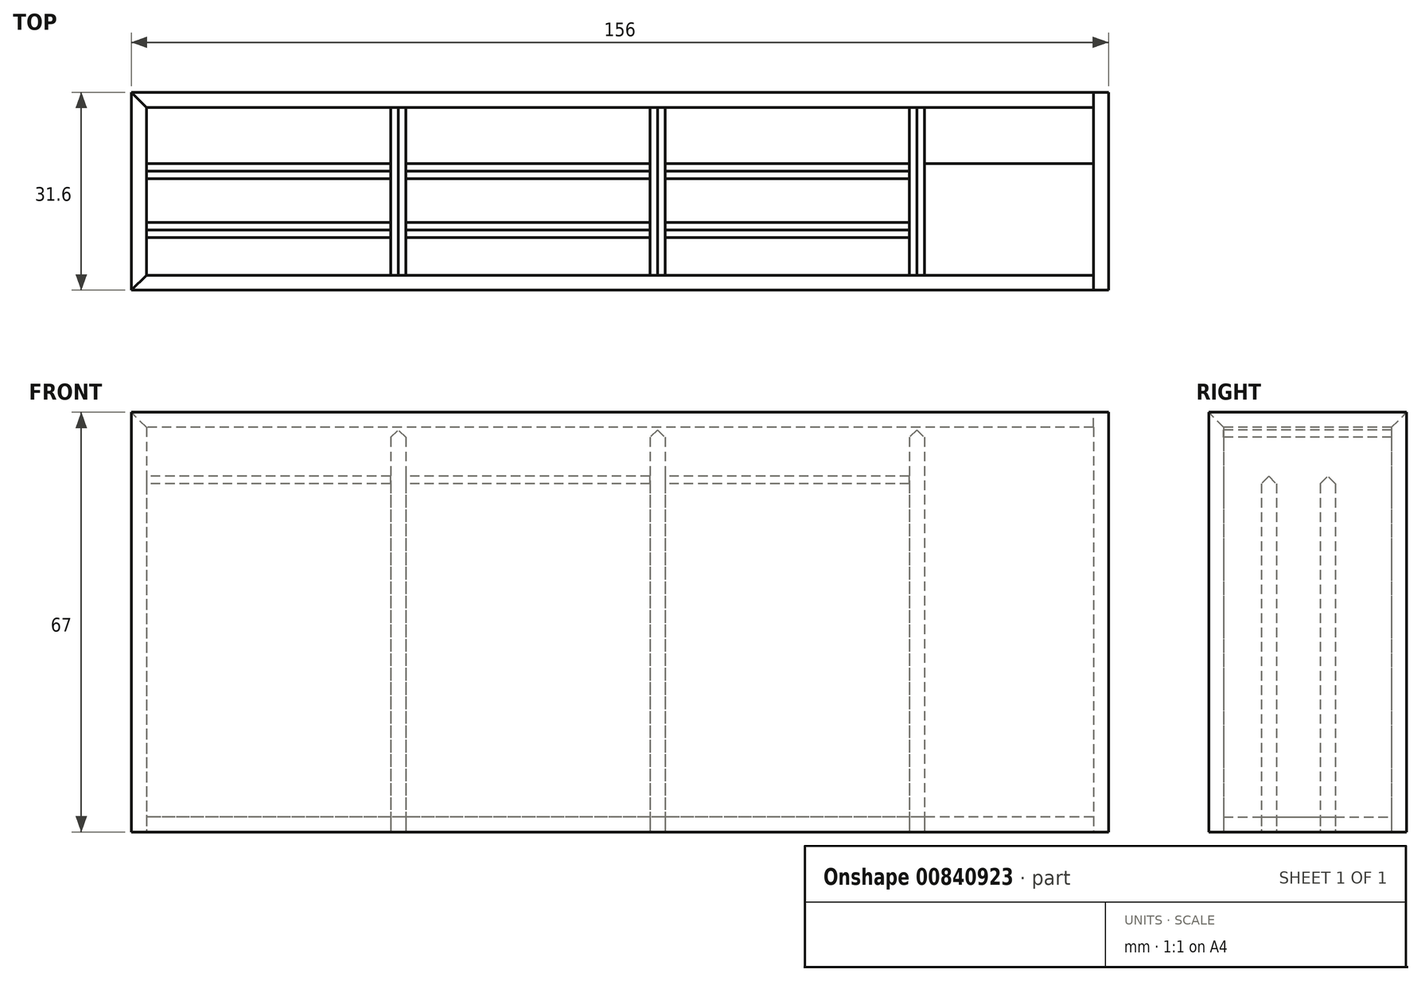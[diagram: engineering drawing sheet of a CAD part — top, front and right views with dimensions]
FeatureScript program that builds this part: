
annotation { "Feature Type Name" : "Feature", "Feature Type Description" : "" }
export const myFeature = defineFeature(function(context is Context, id is Id, definition is map)
    precondition{}
    {
        {
            var Q0;
            Q0=qCreatedBy(makeId("Top.planeOp"),FACE);
            var sketch = newSketch(context, id + "F0", { "sketchPlane" : qUnion([Q0])});
            skLineSegment(sketch, "E0.bottom", {"start": v(78, -15.8) * mm, "end": v(-78, -15.8) * mm});
            skLineSegment(sketch, "E0.top", {"start": v(78, 15.8) * mm, "end": v(-78, 15.8) * mm});
            skLineSegment(sketch, "E0.left", {"start": v(78, -15.8) * mm, "end": v(78, 15.8) * mm});
            skLineSegment(sketch, "E0.right", {"start": v(-78, -15.8) * mm, "end": v(-78, 15.8) * mm});
            skLineSegment(sketch, "E1.0", {"start": v(75.6, 13.4) * mm, "end": v(-75.6, 13.4) * mm});
            skLineSegment(sketch, "E1.1", {"start": v(75.6, -13.4) * mm, "end": v(75.6, 13.4) * mm});
            skLineSegment(sketch, "E1.2", {"start": v(75.6, -13.4) * mm, "end": v(-75.6, -13.4) * mm});
            skLineSegment(sketch, "E1.3", {"start": v(-75.6, -13.4) * mm, "end": v(-75.6, 13.4) * mm});
            skLineSegment(sketch, "E2.0", {"start": v(-36.6, -13.4) * mm, "end": v(-36.6, 13.4) * mm});
            skLineSegment(sketch, "E3.0", {"start": v(-34.2, -13.4) * mm, "end": v(-34.2, 13.4) * mm});
            skLineSegment(sketch, "E4.0", {"start": v(4.8, -13.4) * mm, "end": v(4.8, 13.4) * mm});
            skLineSegment(sketch, "E5.0", {"start": v(7.2, -13.4) * mm, "end": v(7.2, 13.4) * mm});
            skLineSegment(sketch, "E6.0", {"start": v(46.2, -13.4) * mm, "end": v(46.2, 13.4) * mm});
            skLineSegment(sketch, "E7.0", {"start": v(48.6, -13.4) * mm, "end": v(48.6, 13.4) * mm});
            skLineSegment(sketch, "E8", {"start": v(48.6, 13.4) * mm, "end": v(75.6, 13.4) * mm});
            skLineSegment(sketch, "E9.0", {"start": v(75.6, -7.4) * mm, "end": v(-75.6, -7.4) * mm});
            skLineSegment(sketch, "E10.0", {"start": v(75.6, -5) * mm, "end": v(-75.6, -5) * mm});
            skLineSegment(sketch, "E11.0", {"start": v(75.6, 2) * mm, "end": v(-75.6, 2) * mm});
            skLineSegment(sketch, "E12.0", {"start": v(75.6, 4.4) * mm, "end": v(-75.6, 4.4) * mm});
            skLineSegment(sketch, "E13", {"start": v(75.6, 13.4) * mm, "end": v(75.6, -13.4) * mm});
            skSolve(sketch);
        }
        {
            var Q0;
            Q0=makeQuery(id+"F0.imprint","IMPRINT",FACE,{"disambiguationData":[TD([[makeQuery(id+"F0.imprint","IMPRINT",EDGE,{"derivedFrom":sQuery(id+"F0.wireOp",EDGE,"E0.bottom")}),-1.0]])]});
            extrude(context, id + "F1", {"entities" : qUnion([Q0]), "depth" : 67 * mm, "offsetDistance" : 25 * mm});
        }
        {
            var Q0;
            {var subQ0=sQuery(id+"F0.wireOp",EDGE,"E6.0");var subQ1=sQuery(id+"F0.wireOp",EDGE,"E1.2");var subQ2=makeQuery(id+"F0.imprint","INTERSECT",VERTEX,{"derivedFrom":[subQ1,subQ0]});Q0=makeQuery(id+"F0.imprint","IMPRINT",FACE,{"disambiguationData":[TD([[makeQuery(id+"F0.imprint","IMPRINT",EDGE,{"disambiguationData":[TD([[subQ2,1.0]])],"derivedFrom":subQ1}),-1.0]])]});}
            var Q1;
            {var subQ0=sQuery(id+"F0.wireOp",EDGE,"E9.0");var subQ1=sQuery(id+"F0.wireOp",EDGE,"E6.0");var subQ2=makeQuery(id+"F0.imprint","INTERSECT",VERTEX,{"derivedFrom":[subQ1,subQ0]});Q1=makeQuery(id+"F0.imprint","IMPRINT",FACE,{"disambiguationData":[TD([[makeQuery(id+"F0.imprint","IMPRINT",EDGE,{"disambiguationData":[TD([[subQ2,-1.0]])],"derivedFrom":subQ1}),-1.0]])]});}
            var Q2;
            {var subQ0=sQuery(id+"F0.wireOp",EDGE,"E10.0");var subQ1=sQuery(id+"F0.wireOp",EDGE,"E6.0");var subQ2=makeQuery(id+"F0.imprint","INTERSECT",VERTEX,{"derivedFrom":[subQ1,subQ0]});Q2=makeQuery(id+"F0.imprint","IMPRINT",FACE,{"disambiguationData":[TD([[makeQuery(id+"F0.imprint","IMPRINT",EDGE,{"disambiguationData":[TD([[subQ2,-1.0]])],"derivedFrom":subQ1}),-1.0]])]});}
            var Q3;
            {var subQ0=sQuery(id+"F0.wireOp",EDGE,"E11.0");var subQ1=sQuery(id+"F0.wireOp",EDGE,"E6.0");var subQ2=makeQuery(id+"F0.imprint","INTERSECT",VERTEX,{"derivedFrom":[subQ1,subQ0]});Q3=makeQuery(id+"F0.imprint","IMPRINT",FACE,{"disambiguationData":[TD([[makeQuery(id+"F0.imprint","IMPRINT",EDGE,{"disambiguationData":[TD([[subQ2,-1.0]])],"derivedFrom":subQ1}),-1.0]])]});}
            var Q4;
            {var subQ1=sQuery(id+"F0.wireOp",EDGE,"E1.0");var subQ3=sQuery(id+"F0.wireOp",EDGE,"E6.0");var subQ4=makeQuery(id+"F0.imprint","INTERSECT",VERTEX,{"derivedFrom":[subQ1,subQ3]});Q4=makeQuery(id+"F0.imprint","IMPRINT",FACE,{"disambiguationData":[TD([[makeQuery(id+"F0.imprint","IMPRINT",EDGE,{"disambiguationData":[TD([[subQ4,1.0]])],"derivedFrom":subQ3}),-1.0]])]});}
            var Q5;
            {var subQ0=sQuery(id+"F0.wireOp",EDGE,"E4.0");var subQ1=sQuery(id+"F0.wireOp",EDGE,"E1.0");var subQ2=makeQuery(id+"F0.imprint","INTERSECT",VERTEX,{"derivedFrom":[subQ1,subQ0]});Q5=makeQuery(id+"F0.imprint","IMPRINT",FACE,{"disambiguationData":[TD([[makeQuery(id+"F0.imprint","IMPRINT",EDGE,{"disambiguationData":[TD([[subQ2,1.0]])],"derivedFrom":subQ1}),1.0]])]});}
            var Q6;
            {var subQ0=sQuery(id+"F0.wireOp",EDGE,"E11.0");var subQ1=sQuery(id+"F0.wireOp",EDGE,"E4.0");var subQ2=makeQuery(id+"F0.imprint","INTERSECT",VERTEX,{"derivedFrom":[subQ1,subQ0]});Q6=makeQuery(id+"F0.imprint","IMPRINT",FACE,{"disambiguationData":[TD([[makeQuery(id+"F0.imprint","IMPRINT",EDGE,{"disambiguationData":[TD([[subQ2,-1.0]])],"derivedFrom":subQ1}),-1.0]])]});}
            var Q7;
            {var subQ0=sQuery(id+"F0.wireOp",EDGE,"E10.0");var subQ1=sQuery(id+"F0.wireOp",EDGE,"E4.0");var subQ2=makeQuery(id+"F0.imprint","INTERSECT",VERTEX,{"derivedFrom":[subQ1,subQ0]});Q7=makeQuery(id+"F0.imprint","IMPRINT",FACE,{"disambiguationData":[TD([[makeQuery(id+"F0.imprint","IMPRINT",EDGE,{"disambiguationData":[TD([[subQ2,-1.0]])],"derivedFrom":subQ1}),-1.0]])]});}
            var Q8;
            {var subQ0=sQuery(id+"F0.wireOp",EDGE,"E9.0");var subQ1=sQuery(id+"F0.wireOp",EDGE,"E4.0");var subQ2=makeQuery(id+"F0.imprint","INTERSECT",VERTEX,{"derivedFrom":[subQ1,subQ0]});Q8=makeQuery(id+"F0.imprint","IMPRINT",FACE,{"disambiguationData":[TD([[makeQuery(id+"F0.imprint","IMPRINT",EDGE,{"disambiguationData":[TD([[subQ2,-1.0]])],"derivedFrom":subQ1}),-1.0]])]});}
            var Q9;
            {var subQ0=sQuery(id+"F0.wireOp",EDGE,"E4.0");var subQ1=sQuery(id+"F0.wireOp",EDGE,"E1.2");var subQ2=makeQuery(id+"F0.imprint","INTERSECT",VERTEX,{"derivedFrom":[subQ1,subQ0]});Q9=makeQuery(id+"F0.imprint","IMPRINT",FACE,{"disambiguationData":[TD([[makeQuery(id+"F0.imprint","IMPRINT",EDGE,{"disambiguationData":[TD([[subQ2,1.0]])],"derivedFrom":subQ1}),-1.0]])]});}
            var Q10;
            {var subQ0=sQuery(id+"F0.wireOp",EDGE,"E2.0");var subQ1=sQuery(id+"F0.wireOp",EDGE,"E1.2");var subQ2=makeQuery(id+"F0.imprint","INTERSECT",VERTEX,{"derivedFrom":[subQ1,subQ0]});Q10=makeQuery(id+"F0.imprint","IMPRINT",FACE,{"disambiguationData":[TD([[makeQuery(id+"F0.imprint","IMPRINT",EDGE,{"disambiguationData":[TD([[subQ2,1.0]])],"derivedFrom":subQ1}),-1.0]])]});}
            var Q11;
            {var subQ0=sQuery(id+"F0.wireOp",EDGE,"E9.0");var subQ1=sQuery(id+"F0.wireOp",EDGE,"E2.0");var subQ2=makeQuery(id+"F0.imprint","INTERSECT",VERTEX,{"derivedFrom":[subQ1,subQ0]});Q11=makeQuery(id+"F0.imprint","IMPRINT",FACE,{"disambiguationData":[TD([[makeQuery(id+"F0.imprint","IMPRINT",EDGE,{"disambiguationData":[TD([[subQ2,-1.0]])],"derivedFrom":subQ1}),-1.0]])]});}
            var Q12;
            {var subQ0=sQuery(id+"F0.wireOp",EDGE,"E10.0");var subQ1=sQuery(id+"F0.wireOp",EDGE,"E2.0");var subQ2=makeQuery(id+"F0.imprint","INTERSECT",VERTEX,{"derivedFrom":[subQ1,subQ0]});Q12=makeQuery(id+"F0.imprint","IMPRINT",FACE,{"disambiguationData":[TD([[makeQuery(id+"F0.imprint","IMPRINT",EDGE,{"disambiguationData":[TD([[subQ2,-1.0]])],"derivedFrom":subQ1}),-1.0]])]});}
            var Q13;
            {var subQ0=sQuery(id+"F0.wireOp",EDGE,"E11.0");var subQ1=sQuery(id+"F0.wireOp",EDGE,"E2.0");var subQ2=makeQuery(id+"F0.imprint","INTERSECT",VERTEX,{"derivedFrom":[subQ1,subQ0]});Q13=makeQuery(id+"F0.imprint","IMPRINT",FACE,{"disambiguationData":[TD([[makeQuery(id+"F0.imprint","IMPRINT",EDGE,{"disambiguationData":[TD([[subQ2,-1.0]])],"derivedFrom":subQ1}),-1.0]])]});}
            var Q14;
            {var subQ0=sQuery(id+"F0.wireOp",EDGE,"E2.0");var subQ1=sQuery(id+"F0.wireOp",EDGE,"E1.0");var subQ2=makeQuery(id+"F0.imprint","INTERSECT",VERTEX,{"derivedFrom":[subQ1,subQ0]});Q14=makeQuery(id+"F0.imprint","IMPRINT",FACE,{"disambiguationData":[TD([[makeQuery(id+"F0.imprint","IMPRINT",EDGE,{"disambiguationData":[TD([[subQ2,1.0]])],"derivedFrom":subQ1}),1.0]])]});}
            extrude(context, id + "F2", {"entities" : qUnion([Q0, Q1, Q2, Q3, Q4, Q5, Q6, Q7, Q8, Q9, Q10, Q11, Q12, Q13, Q14]), "depth" : 65.4 * mm, "offsetDistance" : 25 * mm});
        }
        {
            var Q0;
            {var subQ0=sQuery(id+"F0.wireOp",EDGE,"E9.0");var subQ1=sQuery(id+"F0.wireOp",EDGE,"E1.3");var subQ2=makeQuery(id+"F0.imprint","INTERSECT",VERTEX,{"derivedFrom":[subQ1,subQ0]});Q0=makeQuery(id+"F0.imprint","IMPRINT",FACE,{"disambiguationData":[TD([[makeQuery(id+"F0.imprint","IMPRINT",EDGE,{"disambiguationData":[TD([[subQ2,-1.0]])],"derivedFrom":subQ1}),-1.0]])]});}
            var Q1;
            {var subQ0=sQuery(id+"F0.wireOp",EDGE,"E11.0");var subQ1=sQuery(id+"F0.wireOp",EDGE,"E1.3");var subQ2=makeQuery(id+"F0.imprint","INTERSECT",VERTEX,{"derivedFrom":[subQ1,subQ0]});Q1=makeQuery(id+"F0.imprint","IMPRINT",FACE,{"disambiguationData":[TD([[makeQuery(id+"F0.imprint","IMPRINT",EDGE,{"disambiguationData":[TD([[subQ2,-1.0]])],"derivedFrom":subQ1}),-1.0]])]});}
            var Q2;
            {var subQ0=sQuery(id+"F0.wireOp",EDGE,"E9.0");var subQ1=sQuery(id+"F0.wireOp",EDGE,"E3.0");var subQ2=makeQuery(id+"F0.imprint","INTERSECT",VERTEX,{"derivedFrom":[subQ1,subQ0]});Q2=makeQuery(id+"F0.imprint","IMPRINT",FACE,{"disambiguationData":[TD([[makeQuery(id+"F0.imprint","IMPRINT",EDGE,{"disambiguationData":[TD([[subQ2,-1.0]])],"derivedFrom":subQ1}),-1.0]])]});}
            var Q3;
            {var subQ0=sQuery(id+"F0.wireOp",EDGE,"E11.0");var subQ1=sQuery(id+"F0.wireOp",EDGE,"E3.0");var subQ2=makeQuery(id+"F0.imprint","INTERSECT",VERTEX,{"derivedFrom":[subQ1,subQ0]});Q3=makeQuery(id+"F0.imprint","IMPRINT",FACE,{"disambiguationData":[TD([[makeQuery(id+"F0.imprint","IMPRINT",EDGE,{"disambiguationData":[TD([[subQ2,-1.0]])],"derivedFrom":subQ1}),-1.0]])]});}
            var Q4;
            {var subQ0=sQuery(id+"F0.wireOp",EDGE,"E11.0");var subQ1=sQuery(id+"F0.wireOp",EDGE,"E5.0");var subQ2=makeQuery(id+"F0.imprint","INTERSECT",VERTEX,{"derivedFrom":[subQ1,subQ0]});Q4=makeQuery(id+"F0.imprint","IMPRINT",FACE,{"disambiguationData":[TD([[makeQuery(id+"F0.imprint","IMPRINT",EDGE,{"disambiguationData":[TD([[subQ2,-1.0]])],"derivedFrom":subQ1}),-1.0]])]});}
            var Q5;
            {var subQ0=sQuery(id+"F0.wireOp",EDGE,"E9.0");var subQ1=sQuery(id+"F0.wireOp",EDGE,"E5.0");var subQ2=makeQuery(id+"F0.imprint","INTERSECT",VERTEX,{"derivedFrom":[subQ1,subQ0]});Q5=makeQuery(id+"F0.imprint","IMPRINT",FACE,{"disambiguationData":[TD([[makeQuery(id+"F0.imprint","IMPRINT",EDGE,{"disambiguationData":[TD([[subQ2,-1.0]])],"derivedFrom":subQ1}),-1.0]])]});}
            extrude(context, id + "F3", {"entities" : qUnion([Q0, Q1, Q2, Q3, Q4, Q5]), "depth" : 58 * mm, "offsetDistance" : 25 * mm});
        }
        {
            var Q0;
            {var subQ0=sQuery(id+"F0.wireOp",EDGE,"E1.3");var subQ1=sQuery(id+"F0.wireOp",EDGE,"E1.2");var subQ2=makeQuery(id+"F0.imprint","INTERSECT",VERTEX,{"derivedFrom":[subQ1,subQ0]});Q0=makeQuery(id+"F0.imprint","IMPRINT",FACE,{"disambiguationData":[TD([[makeQuery(id+"F0.imprint","IMPRINT",EDGE,{"disambiguationData":[TD([[subQ2,1.0]])],"derivedFrom":subQ1}),-1.0]])]});}
            var Q1;
            {var subQ0=sQuery(id+"F0.wireOp",EDGE,"E10.0");var subQ1=sQuery(id+"F0.wireOp",EDGE,"E1.3");var subQ2=makeQuery(id+"F0.imprint","INTERSECT",VERTEX,{"derivedFrom":[subQ1,subQ0]});Q1=makeQuery(id+"F0.imprint","IMPRINT",FACE,{"disambiguationData":[TD([[makeQuery(id+"F0.imprint","IMPRINT",EDGE,{"disambiguationData":[TD([[subQ2,-1.0]])],"derivedFrom":subQ1}),-1.0]])]});}
            var Q2;
            {var subQ0=sQuery(id+"F0.wireOp",EDGE,"E1.3");var subQ1=sQuery(id+"F0.wireOp",EDGE,"E1.0");var subQ2=makeQuery(id+"F0.imprint","INTERSECT",VERTEX,{"derivedFrom":[subQ1,subQ0]});Q2=makeQuery(id+"F0.imprint","IMPRINT",FACE,{"disambiguationData":[TD([[makeQuery(id+"F0.imprint","IMPRINT",EDGE,{"disambiguationData":[TD([[subQ2,1.0]])],"derivedFrom":subQ1}),1.0]])]});}
            var Q3;
            {var subQ0=sQuery(id+"F0.wireOp",EDGE,"E3.0");var subQ1=sQuery(id+"F0.wireOp",EDGE,"E1.0");var subQ2=makeQuery(id+"F0.imprint","INTERSECT",VERTEX,{"derivedFrom":[subQ1,subQ0]});Q3=makeQuery(id+"F0.imprint","IMPRINT",FACE,{"disambiguationData":[TD([[makeQuery(id+"F0.imprint","IMPRINT",EDGE,{"disambiguationData":[TD([[subQ2,1.0]])],"derivedFrom":subQ1}),1.0]])]});}
            var Q4;
            {var subQ0=sQuery(id+"F0.wireOp",EDGE,"E10.0");var subQ1=sQuery(id+"F0.wireOp",EDGE,"E3.0");var subQ2=makeQuery(id+"F0.imprint","INTERSECT",VERTEX,{"derivedFrom":[subQ1,subQ0]});Q4=makeQuery(id+"F0.imprint","IMPRINT",FACE,{"disambiguationData":[TD([[makeQuery(id+"F0.imprint","IMPRINT",EDGE,{"disambiguationData":[TD([[subQ2,-1.0]])],"derivedFrom":subQ1}),-1.0]])]});}
            var Q5;
            {var subQ0=sQuery(id+"F0.wireOp",EDGE,"E3.0");var subQ1=sQuery(id+"F0.wireOp",EDGE,"E1.2");var subQ2=makeQuery(id+"F0.imprint","INTERSECT",VERTEX,{"derivedFrom":[subQ1,subQ0]});Q5=makeQuery(id+"F0.imprint","IMPRINT",FACE,{"disambiguationData":[TD([[makeQuery(id+"F0.imprint","IMPRINT",EDGE,{"disambiguationData":[TD([[subQ2,1.0]])],"derivedFrom":subQ1}),-1.0]])]});}
            var Q6;
            {var subQ0=sQuery(id+"F0.wireOp",EDGE,"E5.0");var subQ1=sQuery(id+"F0.wireOp",EDGE,"E1.2");var subQ2=makeQuery(id+"F0.imprint","INTERSECT",VERTEX,{"derivedFrom":[subQ1,subQ0]});Q6=makeQuery(id+"F0.imprint","IMPRINT",FACE,{"disambiguationData":[TD([[makeQuery(id+"F0.imprint","IMPRINT",EDGE,{"disambiguationData":[TD([[subQ2,1.0]])],"derivedFrom":subQ1}),-1.0]])]});}
            var Q7;
            {var subQ0=sQuery(id+"F0.wireOp",EDGE,"E10.0");var subQ1=sQuery(id+"F0.wireOp",EDGE,"E5.0");var subQ2=makeQuery(id+"F0.imprint","INTERSECT",VERTEX,{"derivedFrom":[subQ1,subQ0]});Q7=makeQuery(id+"F0.imprint","IMPRINT",FACE,{"disambiguationData":[TD([[makeQuery(id+"F0.imprint","IMPRINT",EDGE,{"disambiguationData":[TD([[subQ2,-1.0]])],"derivedFrom":subQ1}),-1.0]])]});}
            var Q8;
            {var subQ0=sQuery(id+"F0.wireOp",EDGE,"E5.0");var subQ1=sQuery(id+"F0.wireOp",EDGE,"E1.0");var subQ2=makeQuery(id+"F0.imprint","INTERSECT",VERTEX,{"derivedFrom":[subQ1,subQ0]});Q8=makeQuery(id+"F0.imprint","IMPRINT",FACE,{"disambiguationData":[TD([[makeQuery(id+"F0.imprint","IMPRINT",EDGE,{"disambiguationData":[TD([[subQ2,1.0]])],"derivedFrom":subQ1}),1.0]])]});}
            extrude(context, id + "F4", {"entities" : qUnion([Q0, Q1, Q2, Q3, Q4, Q5, Q6, Q7, Q8]), "depth" : 2.4 * mm, "offsetDistance" : 25 * mm});
        }
        {
            var Q0;
            {var subQ0=sQuery(id+"F0.wireOp",EDGE,"E8");Q0=makeQuery(id+"F0.imprint","IMPRINT",FACE,{"disambiguationData":[TD([[makeQuery(id+"F0.imprint","IMPRINT",EDGE,{"derivedFrom":subQ0}),-1.0]])]});}
            var Q1;
            {var subQ0=sQuery(id+"F0.wireOp",EDGE,"E11.0");var subQ1=sQuery(id+"F0.wireOp",EDGE,"E7.0");var subQ2=makeQuery(id+"F0.imprint","INTERSECT",VERTEX,{"derivedFrom":[subQ1,subQ0]});Q1=makeQuery(id+"F0.imprint","IMPRINT",FACE,{"disambiguationData":[TD([[makeQuery(id+"F0.imprint","IMPRINT",EDGE,{"disambiguationData":[TD([[subQ2,-1.0]])],"derivedFrom":subQ1}),-1.0]])]});}
            var Q2;
            {var subQ0=sQuery(id+"F0.wireOp",EDGE,"E10.0");var subQ1=sQuery(id+"F0.wireOp",EDGE,"E7.0");var subQ2=makeQuery(id+"F0.imprint","INTERSECT",VERTEX,{"derivedFrom":[subQ1,subQ0]});Q2=makeQuery(id+"F0.imprint","IMPRINT",FACE,{"disambiguationData":[TD([[makeQuery(id+"F0.imprint","IMPRINT",EDGE,{"disambiguationData":[TD([[subQ2,-1.0]])],"derivedFrom":subQ1}),-1.0]])]});}
            var Q3;
            {var subQ0=sQuery(id+"F0.wireOp",EDGE,"E9.0");var subQ1=sQuery(id+"F0.wireOp",EDGE,"E7.0");var subQ2=makeQuery(id+"F0.imprint","INTERSECT",VERTEX,{"derivedFrom":[subQ1,subQ0]});Q3=makeQuery(id+"F0.imprint","IMPRINT",FACE,{"disambiguationData":[TD([[makeQuery(id+"F0.imprint","IMPRINT",EDGE,{"disambiguationData":[TD([[subQ2,-1.0]])],"derivedFrom":subQ1}),-1.0]])]});}
            var Q4;
            {var subQ0=sQuery(id+"F0.wireOp",EDGE,"E13");var subQ1=sQuery(id+"F0.wireOp",EDGE,"E1.2");var subQ2=makeQuery(id+"F0.imprint","INTERSECT",VERTEX,{"derivedFrom":[subQ1,subQ0]});Q4=makeQuery(id+"F0.imprint","IMPRINT",FACE,{"disambiguationData":[TD([[makeQuery(id+"F0.imprint","IMPRINT",EDGE,{"disambiguationData":[TD([[subQ2,-1.0]])],"derivedFrom":subQ1}),-1.0]])]});}
            extrude(context, id + "F5", {"entities" : qUnion([Q0, Q1, Q2, Q3, Q4]), "depth" : 2.4 * mm, "offsetDistance" : 25 * mm});
        }
        {
            var Q0;
            {var subQ0=sQuery(id+"F0.wireOp",EDGE,"E11.0");Q0=makeQuery(id+"F3.opExtrude","CAP_EDGE",EDGE,{"disambiguationData":[OSD([subQ0]),TDD([makeQuery(id+"F0.imprint","IMPRINT",EDGE,{"disambiguationData":[TD([[makeQuery(id+"F0.imprint","INTERSECT",VERTEX,{"derivedFrom":[sQuery(id+"F0.wireOp",EDGE,"E1.3"),subQ0]}),1.0]])],"derivedFrom":subQ0})])],"isStart":false});}
            var Q1;
            {var subQ0=sQuery(id+"F0.wireOp",EDGE,"E12.0");Q1=makeQuery(id+"F3.opExtrude","CAP_EDGE",EDGE,{"disambiguationData":[OSD([subQ0]),TDD([makeQuery(id+"F0.imprint","IMPRINT",EDGE,{"disambiguationData":[TD([[makeQuery(id+"F0.imprint","INTERSECT",VERTEX,{"derivedFrom":[sQuery(id+"F0.wireOp",EDGE,"E1.3"),subQ0]}),1.0]])],"derivedFrom":subQ0})])],"isStart":false});}
            var Q2;
            {var subQ0=sQuery(id+"F0.wireOp",EDGE,"E10.0");Q2=makeQuery(id+"F3.opExtrude","CAP_EDGE",EDGE,{"disambiguationData":[OSD([subQ0]),TDD([makeQuery(id+"F0.imprint","IMPRINT",EDGE,{"disambiguationData":[TD([[makeQuery(id+"F0.imprint","INTERSECT",VERTEX,{"derivedFrom":[sQuery(id+"F0.wireOp",EDGE,"E1.3"),subQ0]}),1.0]])],"derivedFrom":subQ0})])],"isStart":false});}
            var Q3;
            {var subQ0=sQuery(id+"F0.wireOp",EDGE,"E9.0");Q3=makeQuery(id+"F3.opExtrude","CAP_EDGE",EDGE,{"disambiguationData":[OSD([subQ0]),TDD([makeQuery(id+"F0.imprint","IMPRINT",EDGE,{"disambiguationData":[TD([[makeQuery(id+"F0.imprint","INTERSECT",VERTEX,{"derivedFrom":[sQuery(id+"F0.wireOp",EDGE,"E1.3"),subQ0]}),1.0]])],"derivedFrom":subQ0})])],"isStart":false});}
            var Q4;
            {var subQ0=sQuery(id+"F0.wireOp",EDGE,"E9.0");Q4=makeQuery(id+"F3.opExtrude","CAP_EDGE",EDGE,{"disambiguationData":[OSD([subQ0]),TDD([makeQuery(id+"F0.imprint","IMPRINT",EDGE,{"disambiguationData":[TD([[makeQuery(id+"F0.imprint","INTERSECT",VERTEX,{"derivedFrom":[sQuery(id+"F0.wireOp",EDGE,"E3.0"),subQ0]}),1.0]])],"derivedFrom":subQ0})])],"isStart":false});}
            var Q5;
            {var subQ0=sQuery(id+"F0.wireOp",EDGE,"E10.0");Q5=makeQuery(id+"F3.opExtrude","CAP_EDGE",EDGE,{"disambiguationData":[OSD([subQ0]),TDD([makeQuery(id+"F0.imprint","IMPRINT",EDGE,{"disambiguationData":[TD([[makeQuery(id+"F0.imprint","INTERSECT",VERTEX,{"derivedFrom":[sQuery(id+"F0.wireOp",EDGE,"E3.0"),subQ0]}),1.0]])],"derivedFrom":subQ0})])],"isStart":false});}
            var Q6;
            {var subQ0=sQuery(id+"F0.wireOp",EDGE,"E12.0");Q6=makeQuery(id+"F3.opExtrude","CAP_EDGE",EDGE,{"disambiguationData":[OSD([subQ0]),TDD([makeQuery(id+"F0.imprint","IMPRINT",EDGE,{"disambiguationData":[TD([[makeQuery(id+"F0.imprint","INTERSECT",VERTEX,{"derivedFrom":[sQuery(id+"F0.wireOp",EDGE,"E3.0"),subQ0]}),1.0]])],"derivedFrom":subQ0})])],"isStart":false});}
            var Q7;
            {var subQ0=sQuery(id+"F0.wireOp",EDGE,"E11.0");Q7=makeQuery(id+"F3.opExtrude","CAP_EDGE",EDGE,{"disambiguationData":[OSD([subQ0]),TDD([makeQuery(id+"F0.imprint","IMPRINT",EDGE,{"disambiguationData":[TD([[makeQuery(id+"F0.imprint","INTERSECT",VERTEX,{"derivedFrom":[sQuery(id+"F0.wireOp",EDGE,"E3.0"),subQ0]}),1.0]])],"derivedFrom":subQ0})])],"isStart":false});}
            var Q8;
            {var subQ0=sQuery(id+"F0.wireOp",EDGE,"E11.0");Q8=makeQuery(id+"F3.opExtrude","CAP_EDGE",EDGE,{"disambiguationData":[OSD([subQ0]),TDD([makeQuery(id+"F0.imprint","IMPRINT",EDGE,{"disambiguationData":[TD([[makeQuery(id+"F0.imprint","INTERSECT",VERTEX,{"derivedFrom":[sQuery(id+"F0.wireOp",EDGE,"E5.0"),subQ0]}),1.0]])],"derivedFrom":subQ0})])],"isStart":false});}
            var Q9;
            {var subQ0=sQuery(id+"F0.wireOp",EDGE,"E12.0");Q9=makeQuery(id+"F3.opExtrude","CAP_EDGE",EDGE,{"disambiguationData":[OSD([subQ0]),TDD([makeQuery(id+"F0.imprint","IMPRINT",EDGE,{"disambiguationData":[TD([[makeQuery(id+"F0.imprint","INTERSECT",VERTEX,{"derivedFrom":[sQuery(id+"F0.wireOp",EDGE,"E5.0"),subQ0]}),1.0]])],"derivedFrom":subQ0})])],"isStart":false});}
            var Q10;
            {var subQ0=sQuery(id+"F0.wireOp",EDGE,"E9.0");Q10=makeQuery(id+"F3.opExtrude","CAP_EDGE",EDGE,{"disambiguationData":[OSD([subQ0]),TDD([makeQuery(id+"F0.imprint","IMPRINT",EDGE,{"disambiguationData":[TD([[makeQuery(id+"F0.imprint","INTERSECT",VERTEX,{"derivedFrom":[sQuery(id+"F0.wireOp",EDGE,"E5.0"),subQ0]}),1.0]])],"derivedFrom":subQ0})])],"isStart":false});}
            var Q11;
            {var subQ0=sQuery(id+"F0.wireOp",EDGE,"E10.0");Q11=makeQuery(id+"F3.opExtrude","CAP_EDGE",EDGE,{"disambiguationData":[OSD([subQ0]),TDD([makeQuery(id+"F0.imprint","IMPRINT",EDGE,{"disambiguationData":[TD([[makeQuery(id+"F0.imprint","INTERSECT",VERTEX,{"derivedFrom":[sQuery(id+"F0.wireOp",EDGE,"E5.0"),subQ0]}),1.0]])],"derivedFrom":subQ0})])],"isStart":false});}
            var Q12;
            Q12=makeQuery(id+"F1.opExtrude","CAP_EDGE",EDGE,{"disambiguationData":[OSD([sQuery(id+"F0.wireOp",EDGE,"E1.0"),sQuery(id+"F0.wireOp",EDGE,"E8")])],"isStart":false});
            var Q13;
            Q13=makeQuery(id+"F1.opExtrude","CAP_EDGE",EDGE,{"disambiguationData":[OSD([sQuery(id+"F0.wireOp",EDGE,"E1.2")])],"isStart":false});
            var Q14;
            Q14=makeQuery(id+"F1.opExtrude","CAP_EDGE",EDGE,{"disambiguationData":[OSD([sQuery(id+"F0.wireOp",EDGE,"E1.3")])],"isStart":false});
            var Q15;
            Q15=makeQuery(id+"F1.opExtrude","CAP_EDGE",EDGE,{"disambiguationData":[OSD([sQuery(id+"F0.wireOp",EDGE,"E13")])],"isStart":false});
            var Q16;
            Q16=makeQuery(id+"F2.opExtrude","CAP_EDGE",EDGE,{"disambiguationData":[OSD([sQuery(id+"F0.wireOp",EDGE,"E2.0")])],"isStart":false});
            var Q17;
            Q17=makeQuery(id+"F2.opExtrude","CAP_EDGE",EDGE,{"disambiguationData":[OSD([sQuery(id+"F0.wireOp",EDGE,"E3.0")])],"isStart":false});
            var Q18;
            Q18=makeQuery(id+"F2.opExtrude","CAP_EDGE",EDGE,{"disambiguationData":[OSD([sQuery(id+"F0.wireOp",EDGE,"E4.0")])],"isStart":false});
            var Q19;
            Q19=makeQuery(id+"F2.opExtrude","CAP_EDGE",EDGE,{"disambiguationData":[OSD([sQuery(id+"F0.wireOp",EDGE,"E5.0")])],"isStart":false});
            var Q20;
            Q20=makeQuery(id+"F2.opExtrude","CAP_EDGE",EDGE,{"disambiguationData":[OSD([sQuery(id+"F0.wireOp",EDGE,"E6.0")])],"isStart":false});
            var Q21;
            Q21=makeQuery(id+"F2.opExtrude","CAP_EDGE",EDGE,{"disambiguationData":[OSD([sQuery(id+"F0.wireOp",EDGE,"E7.0")])],"isStart":false});
            chamfer(context, id + "F6", {"entities" : qUnion([Q0, Q1, Q2, Q3, Q4, Q5, Q6, Q7, Q8, Q9, Q10, Q11, Q12, Q13, Q14, Q15, Q16, Q17, Q18, Q19, Q20, Q21]), "width" : 2.4 * mm, "tangentPropagation" : true});
        }
    });
